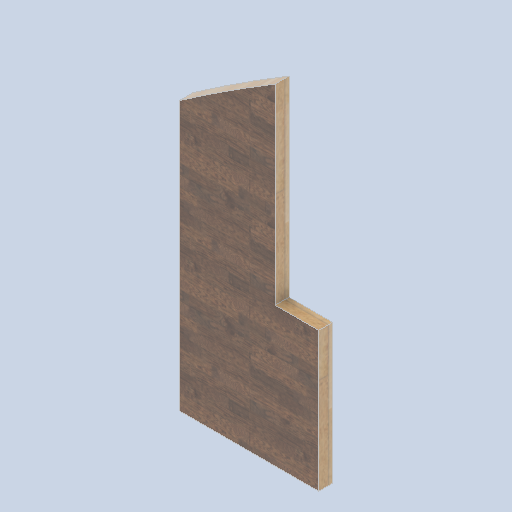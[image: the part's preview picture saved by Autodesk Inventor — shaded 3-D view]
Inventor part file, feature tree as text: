
AUTODESK INVENTOR PART (.ipt)
format: ipt  version: 2024.2 (Build 282272000, 272)  size: 174,080 bytes
history: native  units: in
note: dims shown in document units (in); Inventor stores cm internally (conversion verified against a paired STEP export)
features: other x3, sketch x1
ambient origin geometry x8: Origin, YZ Plane, XZ Plane, XY Plane, X Axis, Y Axis, Z Axis, Center Point
bodies: Solid1 (feature_tree)
feature tree (4):
  other  "front_wall_block03.ipt"
  other  "Solid1::front_wall_block03.ipt"
  other  "TaggingFeature1"
  sketch  "Sketch1"  dims[d0=0.3937in]
